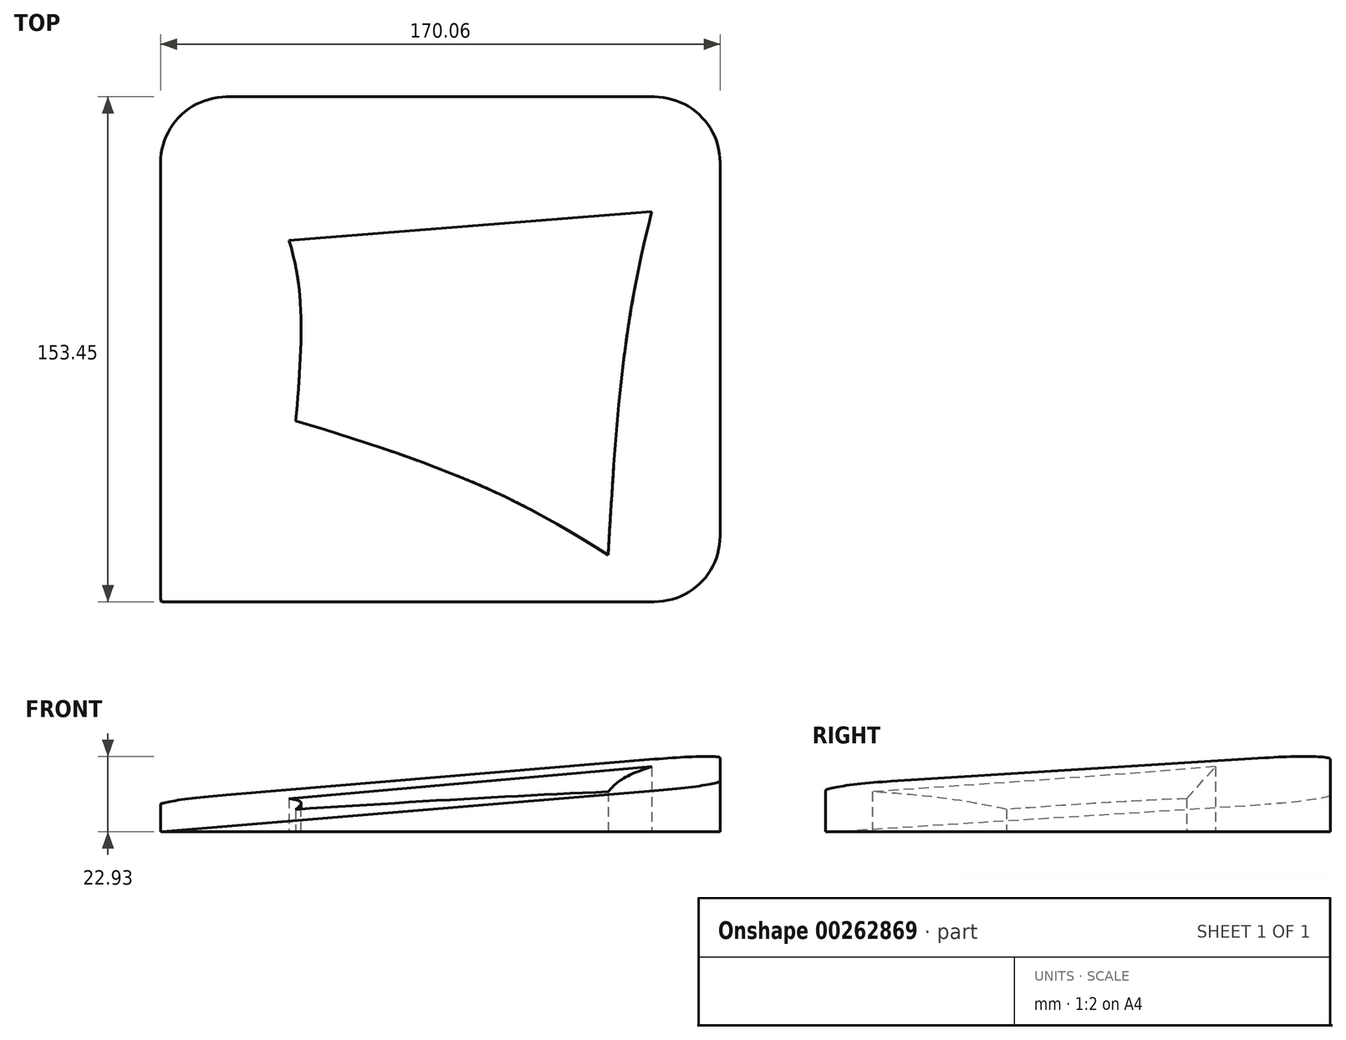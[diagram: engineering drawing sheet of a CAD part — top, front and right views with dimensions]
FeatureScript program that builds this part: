
annotation { "Feature Type Name" : "Feature", "Feature Type Description" : "" }
export const myFeature = defineFeature(function(context is Context, id is Id, definition is map)
    precondition{}
    {
        {
            var Q0;
            Q0=qCreatedBy(makeId("Top.planeOp"),FACE);
            var sketch = newSketch(context, id + "F0", { "sketchPlane" : qUnion([Q0])});
            skFitSpline(sketch, "E0", {"points": [v(-62.3, 46.3) * mm, v(-49.8, 12.42) * mm, v(-50.08, -32.78) * mm], "startDerivative": vector(32.85, -68.53) * mm, "endDerivative": vector(-7.65, -89.25) * mm});
            skFitSpline(sketch, "E1", {"points": [v(-50.08, -32.78) * mm, v(-3.93, -48.31) * mm, v(44.81, -73.56) * mm], "startDerivative": vector(95.28, -27.9) * mm, "endDerivative": vector(117.64, -75.15) * mm});
            skFitSpline(sketch, "E2", {"points": [v(-62.3, 46.3) * mm, v(64.89, 56.4) * mm], "startDerivative": vector(127.2, 10.1) * mm, "endDerivative": vector(127.2, 10.1) * mm});
            skFitSpline(sketch, "E3", {"points": [v(64.89, 56.4) * mm, v(51.49, -0.72) * mm, v(44.81, -73.56) * mm], "startDerivative": vector(-32.07, -116.85) * mm, "endDerivative": vector(-8.51, -142.6) * mm});
            skLineSegment(sketch, "E4.bottom", {"start": v(-91.18, 65.69) * mm, "end": v(78.88, 65.69) * mm});
            skLineSegment(sketch, "E4.top", {"start": v(-91.18, -87.76) * mm, "end": v(78.88, -87.76) * mm});
            skLineSegment(sketch, "E4.left", {"start": v(-91.18, 65.69) * mm, "end": v(-91.18, -87.76) * mm});
            skLineSegment(sketch, "E4.right", {"start": v(78.88, 65.69) * mm, "end": v(78.88, -87.76) * mm});
            skSolve(sketch);
        }
        {
            var Q0;
            Q0=makeQuery(id+"F0.imprint","IMPRINT",FACE,{"disambiguationData":[TD([[makeQuery(id+"F0.imprint","IMPRINT",EDGE,{"derivedFrom":sQuery(id+"F0.wireOp",EDGE,"E0")}),-1.0]])]});
            extrude(context, id + "F1", {"entities" : qUnion([Q0]), "depth" : 25 * mm});
        }
        {
            var Q0;
            Q0=makeQuery(id+"F1.opExtrude","SWEPT_FACE",FACE,{"disambiguationData":[OSD([sQuery(id+"F0.wireOp",EDGE,"E2")])]});
            extrude(context, id + "F2", {"entities" : qUnion([Q0]), "operationType" : NewBodyOperationType.ADD, "depth" : 25 * mm});
        }
        {
            var Q0;
            Q0=makeQuery(id+"F1.opExtrude","CAP_EDGE",EDGE,{"disambiguationData":[OSD([sQuery(id+"F0.wireOp",EDGE,"E4.left")])],"isStart":false});
            chamfer(context, id + "F3", {"entities" : qUnion([Q0]), "chamferType" : ChamferType.TWO_OFFSETS, "width1" : 15 * mm, "oppositeDirection" : true, "width2" : 180 * mm, "tangentPropagation" : true});
        }
        {
            var Q0;
            Q0=makeQuery(id+"F3.opChamfer","BLEND_EDGE",EDGE,{"blendedFrom":[makeQuery(id+"F1.opExtrude","CAP_EDGE",EDGE,{"disambiguationData":[OSD([sQuery(id+"F0.wireOp",EDGE,"E4.left")])],"isStart":false}),makeQuery(id+"F1.opExtrude","SWEPT_FACE",FACE,{"disambiguationData":[OSD([sQuery(id+"F0.wireOp",EDGE,"E4.top")])]})],"blendedInto":[makeQuery(id+"F1.opExtrude","SWEPT_FACE",FACE,{"disambiguationData":[OSD([sQuery(id+"F0.wireOp",EDGE,"E4.top")])]})]});
            chamfer(context, id + "F4", {"entities" : qUnion([Q0]), "chamferType" : ChamferType.TWO_OFFSETS, "width1" : 10 * mm, "oppositeDirection" : false, "width2" : 160 * mm, "tangentPropagation" : true});
        }
        {
            var Q0;
            Q0=makeQuery(id+"F1.opExtrude","SWEPT_EDGE",EDGE,{"disambiguationData":[OSD([sQuery(id+"F0.wireOp",EDGE,"E4.top"),sQuery(id+"F0.wireOp",EDGE,"E4.right")])]});
            fillet(context, id + "F5", {"entities" : qUnion([Q0]), "radius" : 20 * mm, "tangentPropagation" : true, "allowEdgeOverflow" : false});
        }
        {
            var Q0;
            Q0=makeQuery(id+"F1.opExtrude","SWEPT_EDGE",EDGE,{"disambiguationData":[OSD([sQuery(id+"F0.wireOp",EDGE,"E4.bottom"),sQuery(id+"F0.wireOp",EDGE,"E4.left")])]});
            fillet(context, id + "F6", {"entities" : qUnion([Q0]), "radius" : 20 * mm, "tangentPropagation" : true, "allowEdgeOverflow" : false});
        }
        {
            var Q0;
            Q0=makeQuery(id+"F1.opExtrude","SWEPT_EDGE",EDGE,{"disambiguationData":[OSD([sQuery(id+"F0.wireOp",EDGE,"E4.bottom"),sQuery(id+"F0.wireOp",EDGE,"E4.right")])]});
            fillet(context, id + "F7", {"entities" : qUnion([Q0]), "radius" : 20 * mm, "tangentPropagation" : true, "allowEdgeOverflow" : false});
        }
    });
